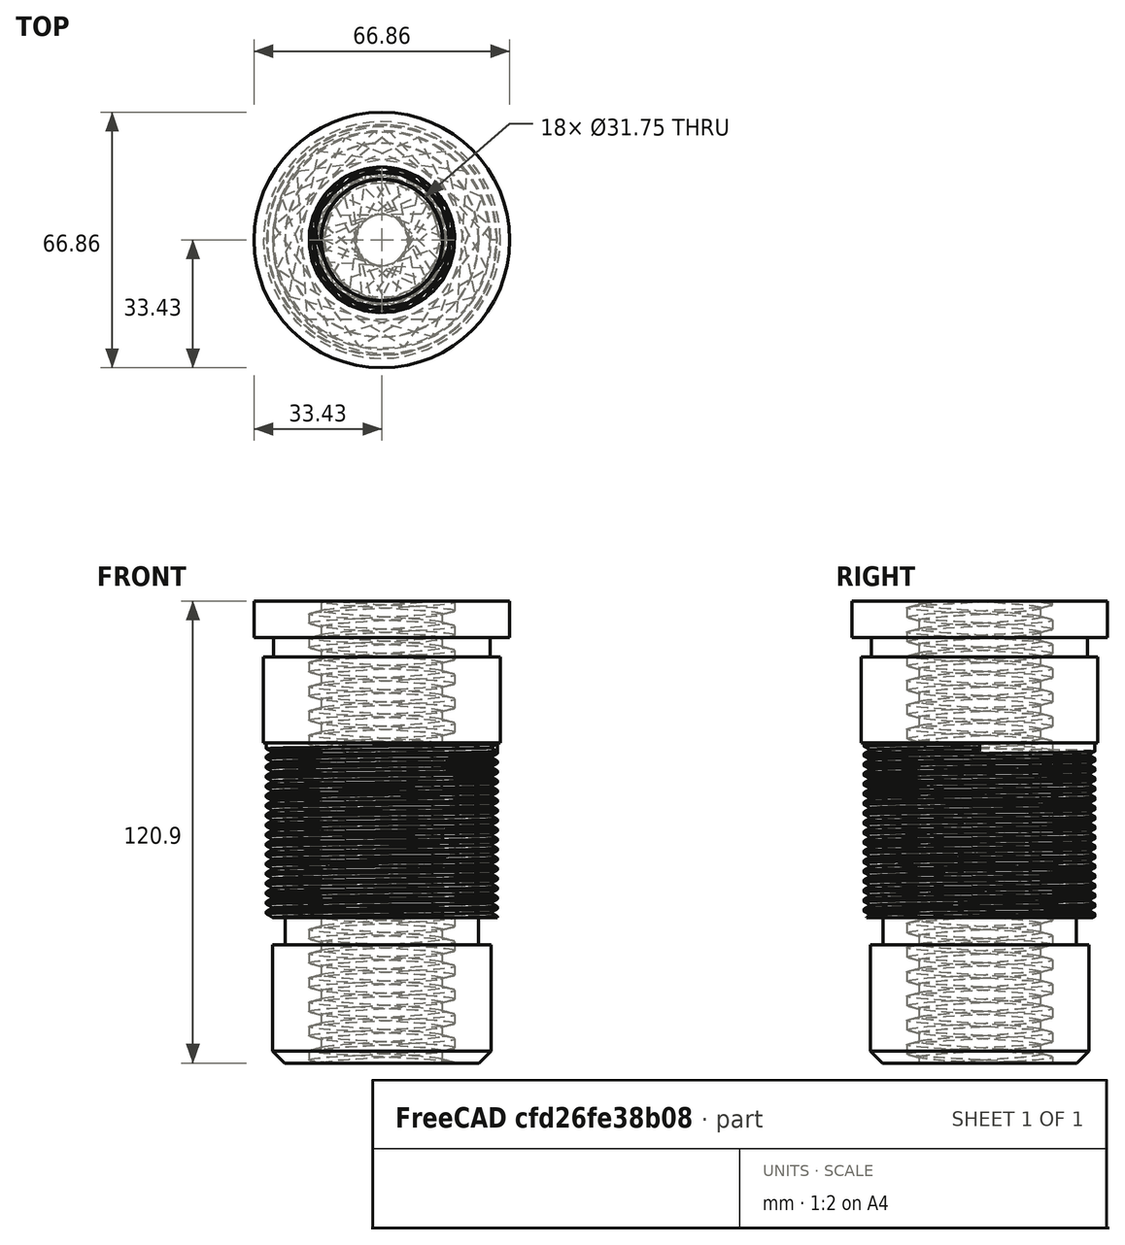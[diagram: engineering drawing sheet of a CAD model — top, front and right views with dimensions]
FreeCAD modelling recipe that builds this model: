
FCSTD DOCUMENT  (FreeCAD 0.21R33771 (Git))
Label: LeadscrewNut
License: All rights reserved
LicenseURL: https://en.wikipedia.org/wiki/All_rights_reserved
objects: TechDraw::DrawViewDimension×12, Sketcher::SketchObject×3, TechDraw::DrawLeaderLine×3, TechDraw::DrawViewAnnotation×3, Part::Helix×2, Part::Sweep×2, Part::Cut×2, PartDesign::Body×1, Part::Revolution×1, Part::Cylinder×1, Part::MultiFuse×1, TechDraw::DrawSVGTemplate×1, TechDraw::DrawViewPart×1, TechDraw::DrawProjGroupItem×1, TechDraw::DrawProjGroup×1, TechDraw::DrawRichAnno×1, TechDraw::DrawPage×1
note: 36 computed .brp shape members not serialized (recipe doc carries the construction recipe); baked Part::Feature solids carry a one-line shape summary decoded from their .brp

FEATURE [Sketcher::SketchObject] Sketch
  FullyConstrained = true
  MapMode = 5
  Placement = pos=(0,0,0) rot=(1,0,0;1.5708rad)
  Support = -> [XZ_Plane]
  sketch-geometry (15):
    g0: LineSegment StartX=0 StartY=120.904 StartZ=0 EndX=33.4327 EndY=120.904 EndZ=0
    g1: LineSegment StartX=33.4327 StartY=120.904 StartZ=0 EndX=33.4327 EndY=111.379 EndZ=0
    g2: LineSegment StartX=33.4327 StartY=111.379 StartZ=0 EndX=28.2575 EndY=111.379 EndZ=0
    g3: LineSegment StartX=28.2575 StartY=111.379 StartZ=0 EndX=28.2575 EndY=106.299 EndZ=0
    g4: LineSegment StartX=28.2575 StartY=106.299 StartZ=0 EndX=30.9499 EndY=106.299 EndZ=0
    g5: LineSegment StartX=30.9499 StartY=106.299 StartZ=0 EndX=30.9499 EndY=83.82 EndZ=0
    g6: LineSegment StartX=30.9499 StartY=83.82 StartZ=0 EndX=30.1625 EndY=83.82 EndZ=0
    g7: LineSegment StartX=30.1625 StartY=83.82 StartZ=0 EndX=30.1625 EndY=38.1 EndZ=0
    g8: LineSegment StartX=30.1625 StartY=38.1 StartZ=0 EndX=25.273 EndY=38.1 EndZ=0
    g9: LineSegment StartX=25.273 StartY=38.1 StartZ=0 EndX=25.273 EndY=30.988 EndZ=0
    g10: LineSegment StartX=25.273 StartY=30.988 StartZ=0 EndX=28.575 EndY=30.988 EndZ=0
    g11: LineSegment StartX=28.575 StartY=30.988 StartZ=0 EndX=28.575 EndY=3.175 EndZ=0
    g12: LineSegment StartX=28.575 StartY=3.175 StartZ=0 EndX=25.4 EndY=0 EndZ=0
    g13: LineSegment StartX=25.4 StartY=0 StartZ=0 EndX=0 EndY=0 EndZ=0
    g14: LineSegment StartX=0 StartY=0 StartZ=0 EndX=0 EndY=120.904 EndZ=0
  constraints (44):
    c: PointOnObject(g0,g-2)
    c: Horizontal(g0)
    c: Coincident(g1,g0)
    c: Vertical(g1)
    c: Coincident(g2,g1)
    c: Horizontal(g2)
    c: Coincident(g3,g2)
    c: Coincident(g4,g3)
    c: Horizontal(g4)
    c: Coincident(g5,g4)
    c: Vertical(g5)
    c: Horizontal(g6)
    c: Vertical(g7)
    c: Coincident(g8,g7)
    c: Horizontal(g8)
    c: Coincident(g9,g8)
    c: Horizontal(g10)
    c: Vertical(g11)
    c: Horizontal(g13)
    c: Coincident(g14,g0)
    c: DistanceX(g0,g0) = 33.4327  'Flange'
    c: Vertical(g3)
    c: DistanceX(g0,g4) = 30.9499  'large journal'
    c: Coincident(g6,g5)
    c: DistanceX(g0,g7) = 30.1625  '2 3/8" - 10TPI thread'
    c: Vertical(g9)
    c: DistanceX(g13,g8) = 25.273  'Small Journal Clearance Groove'
    c: Coincident(g10,g9)
    c: DistanceX(g13,g10) = 28.575  'Small Journal'
    c: Coincident(g11,g10)
    c: Coincident(g12,g11)
    c: Coincident(g13,g12)
    c: Angle(g11,g12) = 2.35619  'chamfer'
    c: DistanceY(g5,g0) = 37.084
    c: Coincident(g7,g6)
    c: DistanceY(g1,g0) = 9.525
    c: DistanceY(g4,g1) = 5.08
    c: DistanceY(g7,g0) = 82.804
    c: DistanceY(g10,g7) = 7.112
    c: DistanceY(g12,g0) = 120.904
    c: DistanceY(g12,g11) = 3.175
    c: Coincident(g14,g13)
    c: Coincident(g13,g-1)
    c: DistanceX(g0,g2) = 28.2575
FEATURE [PartDesign::Body] Body
  Group = -> [Sketch]
  Origin = -> Origin
FEATURE [Part::Revolution] Revolve
  Angle = 360
  Axis = (0,0,1)
  Base = (0,0,0)
  FaceMakerClass = Part::FaceMakerBullseye
  Solid = true
  Source = -> Sketch
  Symmetric = false
FEATURE [Part::Helix] Helix001
  Angle = 0
  AttacherType = Attacher::AttachEngine3D
  Height = 45.72
  LocalCoord = 0
  Pitch = 2.54
  Placement = pos=(0,0,36.83) rot=(0,0,1;0rad)
  Radius = 28.5115
  SegmentLength = 0
  Style = 1
FEATURE [Sketcher::SketchObject] Sketch001
  FullyConstrained = true
  MapMode = 3
  Placement = pos=(0,0,36.83) rot=(1,0,0;1.5708rad)
  Support = -> [Helix001]
  sketch-geometry (3):
    g0: LineSegment StartX=28.5115 StartY=45.72 StartZ=0 EndX=31.8111 EndY=47.625 EndZ=0
    g1: LineSegment StartX=28.5115 StartY=45.72 StartZ=0 EndX=31.8111 EndY=43.815 EndZ=0
    g2: LineSegment StartX=31.8111 StartY=47.625 StartZ=0 EndX=31.8111 EndY=43.815 EndZ=0
  constraints (9):
    c: Coincident(g1,g0)
    c: Coincident(g2,g0)
    c: Coincident(g2,g1)
    c: Angle(g1,g0) = 1.0472
    c: Vertical(g2)
    c: Distance(g0,g0) = 3.81
    c: Equal(g1,g0)
    c: DistanceX(g-1,g0) = 28.5115  'thread minor'
    c: DistanceY(g-1,g0) = 45.72  'thread location'
FEATURE [Part::Sweep] Sweep
  Frenet = true
  Sections = -> [Sketch001]
  Solid = true
  Spine = -> Helix001 [Edge1]
  Transition = 1
FEATURE [Part::Helix] Helix
  Angle = 0
  AttacherType = Attacher::AttachEngine3D
  Height = 146.05
  LocalCoord = 0
  Pitch = 6.35
  Placement = pos=(0,0,-12.7) rot=(0,0,1;0rad)
  Radius = 19.05
  SegmentLength = 0
  Style = 1
FEATURE [Sketcher::SketchObject] Sketch003
  FullyConstrained = true
  MapMode = 3
  Placement = pos=(0,0,0) rot=(1,0,0;1.5708rad)
  sketch-geometry (7):
    g0: LineSegment StartX=19.05 StartY=-15.0473 StartZ=0 EndX=15.8496 EndY=-15.875 EndZ=0
    g1: LineSegment StartX=15.8496 StartY=-15.875 StartZ=0 EndX=15.8496 EndY=-11.8723 EndZ=0
    g2: LineSegment StartX=15.8496 StartY=-11.8723 StartZ=0 EndX=19.05 EndY=-12.7 EndZ=0
    g3: LineSegment StartX=19.05 StartY=-12.7 StartZ=0 EndX=19.05 EndY=-15.0473 EndZ=0
    g4: GeomPoint X=17.4498 Y=-12.2862 Z=0
    g5: GeomPoint X=17.4498 Y=-15.4612 Z=0
    g6: LineSegment StartX=17.4498 StartY=-12.2862 StartZ=0 EndX=17.4498 EndY=-15.4612 EndZ=0
  constraints (18):
    c: Coincident(g1,g0)
    c: Vertical(g1)
    c: Coincident(g2,g1)
    c: Coincident(g3,g2)
    c: Coincident(g3,g0)
    c: Vertical(g3)
    c: DistanceX(g-1,g2) = 19.05
    c: DistanceY(g2,g-1) = 12.7
    c: PointOnObject(g4,g2)
    c: PointOnObject(g5,g0)
    c: Coincident(g6,g4)
    c: Coincident(g6,g5)
    c: Vertical(g6)
    c: DistanceX(g5,g0) = 1.6002
    c: DistanceY(g6,g6) = 3.175
    c: Angle(g2,g0) = 0.506145
    c: Angle(g0,g1) = 1.31772
    c: DistanceX(g0,g0) = 3.2004
FEATURE [Part::Sweep] Sweep001
  Frenet = true
  Sections = -> [Sketch003]
  Solid = true
  Spine = -> Helix [Edge1]
  Transition = 1
FEATURE [Part::Cylinder] Cylinder
  Angle = 360
  AttacherType = Attacher::AttachEngine3D
  FirstAngle = 0
  Height = 152.4
  Placement = pos=(0,0,-19.05) rot=(0,0,1;0rad)
  Radius = 15.875
  SecondAngle = 0
FEATURE [Part::MultiFuse] Fusion
  Shapes = -> [Sweep001,Cylinder]
FEATURE [Part::Cut] Cut
  Base = -> Revolve
  Tool = -> Sweep
FEATURE [Part::Cut] Cut001
  Base = -> Cut
  Tool = -> Fusion
FEATURE [TechDraw::DrawSVGTemplate] Template
  EditableTexts = Designed_by_Name=The Kludge; Drawing_number=00000-00000-001; FC-Date=3/23/2024; FC-SC=1:1; FC-Title=X-axis Leadscrew Nut; Subtitle=Cincinnatti #2 Vertical Mill; Weight=Hefty
  Height = 210
  Orientation = 1
  Template = C:/Program Files/FreeCAD 0.21/data/Mod/TechDraw/Templates/A4_LandscapeTD.svg
  Width = 297
FEATURE [TechDraw::DrawViewPart] View
  CoarseView = false
  Direction = (0.57735,-0.57735,0.57735)
  Focus = 100
  HardHidden = false
  IsoCount = 0
  IsoHidden = false
  IsoVisible = false
  LockPosition = false
  Perspective = false
  Rotation = 0
  ScaleType = 0
  ScrubCount = 0
  SeamHidden = false
  SeamVisible = false
  SmoothHidden = false
  SmoothVisible = true
  Source = -> [Cut001]
  X = 249.293
  XDirection = (0.707107,0.707107,0)
  XSource = -> [XZ_Plane]
  Y = 130.559
FEATURE [TechDraw::DrawProjGroupItem] ProjItem  label="Front"
  CoarseView = false
  Direction = (0,1,0)
  Focus = 100
  HardHidden = false
  IsoCount = 0
  IsoHidden = false
  IsoVisible = false
  LockPosition = true
  Perspective = false
  Rotation = 180
  RotationVector = (0.707107,0.707107,0)
  ScaleType = 2
  ScrubCount = 0
  SeamHidden = false
  SeamVisible = false
  SmoothHidden = false
  SmoothVisible = true
  Source = -> [Cut001]
  Type = 0
  X = 0
  XDirection = (0.707107,0.707107,0)
  Y = 0
FEATURE [TechDraw::DrawProjGroup] ProjGroup
  Anchor = -> ProjItem
  AutoDistribute = true
  LockPosition = false
  ProjectionType = 0
  Rotation = 0
  ScaleType = 0
  Source = -> [Cut001]
  Views = -> [ProjItem]
  X = 90.6792
  Y = 129.277
  spacingX = 15.0012
  spacingY = 15.0012
FEATURE [TechDraw::DrawViewDimension] Dimension001
  AngleOverride = false
  Arbitrary = false
  ArbitraryTolerances = false
  EqualTolerance = true
  ExtensionAngle = 0
  FormatSpec = %.3w
  FormatSpecOverTolerance = %+.2w
  FormatSpecUnderTolerance = %+.2w
  Inverted = false
  LineAngle = 0
  LockPosition = false
  MeasureType = 1
  OverTolerance = 0
  References2D = -> [ProjItem]
  Rotation = 0
  ScaleType = 0
  TheoreticalExact = false
  Type = 2
  UnderTolerance = 0
  X = -41.6505
  Y = 57.309
FEATURE [TechDraw::DrawViewDimension] Dimension003
  AngleOverride = false
  Arbitrary = false
  ArbitraryTolerances = false
  EqualTolerance = true
  ExtensionAngle = 0
  FormatSpec = %.w
  FormatSpecOverTolerance = %+.2w
  FormatSpecUnderTolerance = %+.2w
  Inverted = false
  LineAngle = 0
  LockPosition = false
  MeasureType = 1
  OverTolerance = 0
  References2D = -> [ProjItem]
  Rotation = 0
  ScaleType = 0
  TheoreticalExact = false
  Type = 2
  UnderTolerance = 0
  X = -38.0611
  Y = 50.0065
FEATURE [TechDraw::DrawViewDimension] Dimension
  AngleOverride = false
  Arbitrary = false
  ArbitraryTolerances = false
  EqualTolerance = true
  ExtensionAngle = 0
  FormatSpec = %.3w
  FormatSpecOverTolerance = %+.2w
  FormatSpecUnderTolerance = %+.2w
  Inverted = false
  LineAngle = 0
  LockPosition = false
  MeasureType = 1
  OverTolerance = 0
  References2D = -> [ProjItem]
  Rotation = 0
  ScaleType = 0
  TheoreticalExact = false
  Type = 2
  UnderTolerance = 0
  X = -50.9512
  Y = 45.5091
FEATURE [TechDraw::DrawViewDimension] Dimension004
  AngleOverride = false
  Arbitrary = false
  ArbitraryTolerances = false
  EqualTolerance = true
  ExtensionAngle = 0
  FormatSpec = %.3w
  FormatSpecOverTolerance = %+.2w
  FormatSpecUnderTolerance = %+.2w
  Inverted = false
  LineAngle = 0
  LockPosition = false
  MeasureType = 1
  OverTolerance = 0
  References2D = -> [ProjItem]
  Rotation = 0
  ScaleType = 0
  TheoreticalExact = false
  Type = 2
  UnderTolerance = 0
  X = -58.5098
  Y = 20.32
FEATURE [TechDraw::DrawViewDimension] Dimension005
  AngleOverride = false
  Arbitrary = false
  ArbitraryTolerances = false
  EqualTolerance = true
  ExtensionAngle = 0
  FormatSpec = %.2w
  FormatSpecOverTolerance = %+.2w
  FormatSpecUnderTolerance = %+.2w
  Inverted = false
  LineAngle = 0
  LockPosition = false
  MeasureType = 1
  OverTolerance = 0
  References2D = -> [ProjItem]
  Rotation = 0
  ScaleType = 0
  TheoreticalExact = false
  Type = 2
  UnderTolerance = 0
  X = -38.9032
  Y = -31.6447
FEATURE [TechDraw::DrawViewDimension] Dimension006
  AngleOverride = false
  Arbitrary = false
  ArbitraryTolerances = false
  EqualTolerance = true
  ExtensionAngle = 0
  FormatSpec = %.3w
  FormatSpecOverTolerance = %+.2w
  FormatSpecUnderTolerance = %+.2w
  Inverted = false
  LineAngle = 0
  LockPosition = false
  MeasureType = 1
  OverTolerance = 0
  References2D = -> [ProjItem]
  Rotation = 0
  ScaleType = 0
  TheoreticalExact = false
  Type = 2
  UnderTolerance = 0
  X = -35.1243
  Y = -50.3618
FEATURE [TechDraw::DrawViewDimension] Dimension007
  AngleOverride = false
  Arbitrary = false
  ArbitraryTolerances = false
  EqualTolerance = true
  ExtensionAngle = 0
  FormatSpec = %.3w
  FormatSpecOverTolerance = %+.2w
  FormatSpecUnderTolerance = %+.2w
  Inverted = false
  LineAngle = 0
  LockPosition = false
  MeasureType = 1
  OverTolerance = 0
  References2D = -> [ProjItem]
  Rotation = 0
  ScaleType = 0
  TheoreticalExact = false
  Type = 2
  UnderTolerance = 0
  X = -69.6484
  Y = -1.44227
FEATURE [TechDraw::DrawViewDimension] Dimension009
  AngleOverride = false
  Arbitrary = false
  ArbitraryTolerances = false
  EqualTolerance = true
  ExtensionAngle = 0
  FormatSpec = %.3w
  FormatSpecOverTolerance = %+.3w
  FormatSpecUnderTolerance = %+.3w
  Inverted = false
  LineAngle = 0
  LockPosition = false
  MeasureType = 1
  OverTolerance = 0
  References2D = -> [ProjItem]
  Rotation = 0
  ScaleType = 0
  TheoreticalExact = false
  Type = 1
  UnderTolerance = 0
  X = 0.452045
  Y = 68.9547
FEATURE [TechDraw::DrawViewDimension] Dimension010
  AngleOverride = false
  Arbitrary = false
  ArbitraryTolerances = false
  EqualTolerance = true
  ExtensionAngle = 0
  FormatSpec = %.3w
  FormatSpecOverTolerance = %+.3w
  FormatSpecUnderTolerance = %+.3w
  Inverted = false
  LineAngle = 0
  LockPosition = false
  MeasureType = 1
  OverTolerance = 0
  References2D = -> [ProjItem]
  Rotation = 0
  ScaleType = 0
  TheoreticalExact = false
  Type = 1
  UnderTolerance = 0
  X = 46.1086
  Y = 52.197
FEATURE [TechDraw::DrawViewDimension] Dimension011
  AngleOverride = false
  Arbitrary = false
  ArbitraryTolerances = false
  EqualTolerance = true
  ExtensionAngle = 0
  FormatSpec = %.3w
  FormatSpecOverTolerance = %+.3w
  FormatSpecUnderTolerance = %+.3w
  Inverted = false
  LineAngle = 0
  LockPosition = false
  MeasureType = 1
  OverTolerance = 0
  References2D = -> [ProjItem]
  Rotation = 0
  ScaleType = 0
  TheoreticalExact = false
  Type = 1
  UnderTolerance = 0
  X = 46.7866
  Y = 39.2062
FEATURE [TechDraw::DrawViewDimension] Dimension012
  AngleOverride = false
  Arbitrary = false
  ArbitraryTolerances = false
  EqualTolerance = true
  ExtensionAngle = 0
  FormatSpec = %.3w
  FormatSpecOverTolerance = %+.3w
  FormatSpecUnderTolerance = %+.3w
  Inverted = false
  LineAngle = 0
  LockPosition = false
  MeasureType = 1
  OverTolerance = 0
  References2D = -> [ProjItem]
  Rotation = 0
  ScaleType = 0
  TheoreticalExact = false
  Type = 1
  UnderTolerance = 0
  X = 45.2045
  Y = -21.8654
FEATURE [TechDraw::DrawViewDimension] Dimension013
  AngleOverride = false
  Arbitrary = false
  ArbitraryTolerances = false
  EqualTolerance = true
  ExtensionAngle = 0
  FormatSpec = %.3w
  FormatSpecOverTolerance = %+.3w
  FormatSpecUnderTolerance = %+.3w
  Inverted = false
  LineAngle = 0
  LockPosition = false
  MeasureType = 1
  OverTolerance = 0
  References2D = -> [ProjItem]
  Rotation = 0
  ScaleType = 0
  TheoreticalExact = false
  Type = 1
  UnderTolerance = 0
  X = 43.8483
  Y = -40.8513
FEATURE [TechDraw::DrawLeaderLine] LeaderLine
  AutoHorizontal = true
  EndSymbol = 7
  LeaderParent = -> View
  LockPosition = true
  Rotation = 0
  Scalable = false
  ScaleType = 0
  StartSymbol = 0
  WayPoints = (3) [(0,0,0),(-250.885,198.9,0),(-388.758,198.9,0)]
  X = -12.8735
  Y = 41.2177
FEATURE [TechDraw::DrawViewAnnotation] Annotation
  Font = osifont
  LineSpace = 100
  LockPosition = false
  MaxWidth = -1
  Rotation = 0
  ScaleType = 0
  Text = 2 3/8" - 10 | 60° Thread
  TextSize = 2.54
  TextStyle = 0
  X = 170.65
  Y = 128.28
FEATURE [TechDraw::DrawViewAnnotation] Annotation001
  Font = osifont
  LineSpace = 100
  LockPosition = false
  MaxWidth = -1
  Rotation = 0
  ScaleType = 0
  Text = 1 1/2" - 4 | ACME Thru
  TextSize = 2.54
  TextStyle = 0
  X = 185.568
  Y = 154.273
FEATURE [TechDraw::DrawLeaderLine] LeaderLine001
  AutoHorizontal = true
  EndSymbol = 7
  LeaderParent = -> Annotation
  LockPosition = true
  Rotation = 0
  Scalable = false
  ScaleType = 0
  StartSymbol = 0
  WayPoints = (3) [(0,0,0),(151.435,153.695,0),(359.376,153.695,0)]
  X = -48.3721
  Y = 15.6959
FEATURE [TechDraw::DrawLeaderLine] LeaderLine002
  AutoHorizontal = true
  EndSymbol = 7
  LeaderParent = -> Annotation
  LockPosition = true
  Rotation = 0
  Scalable = false
  ScaleType = 0
  StartSymbol = 0
  WayPoints = (3) [(0,0,0),(-122.052,-99.4498,0),(-375.197,-99.4498,0)]
  X = 48.1395
  Y = -12.7829
FEATURE [TechDraw::DrawViewAnnotation] Annotation004
  Font = osifont
  LineSpace = 100
  LockPosition = false
  MaxWidth = -1
  Rotation = 0
  ScaleType = 0
  Text = Original Material: Cast Iron
  TextSize = 2.54
  TextStyle = 0
  X = 206.747
  Y = 35.5125
FEATURE [TechDraw::DrawRichAnno] RichTextAnnotation
  AnnoText = <!DOCTYPE HTML PUBLIC "-//W3C//DTD HTML 4.0//EN" "http://www.w3.org/TR/REC-html40/strict.dtd">\n<html><head><meta name="qrichtext" content="1" /><style type="text/css">\np, li { white-space: pre-wrap; }\n</style></head><body style=" font-family:'osifont'; font-size:8.25pt; font-weight:400; font-style:normal;">\n<p style=" margin-top:0px; margin-bottom:0px; margin-left:0px; margin-right:0px; -qt-block-indent:0; text-indent:0px;"><span style=" font-size:7pt; color:#000000; background-color:#ffffff;">This drawing is provided without any warranty, free of charge, for any use.  It may be redistributed without restriction, and modified if note of such modifications are made on the resulting drawing.</span></p></body></html>
  LockPosition = false
  MaxWidth = -1
  Rotation = 0
  ScaleType = 0
  ShowFrame = true
  X = 149.814
  Y = 10.5671
FEATURE [TechDraw::DrawPage] Page
  KeepUpdated = true
  NextBalloonIndex = 1
  ProjectionType = 0
  Template = -> Template
  Views = -> [View,ProjGroup,Dimension001,Dimension003,Dimension,Dimension004,Dimension005,Dimension006,Dimension007,Dimension009,Dimension010,Dimension011,Dimension012,Dimension013,LeaderLine,Annotation,Annotation001,LeaderLine001,LeaderLine002,Annotation004,RichTextAnnotation]
